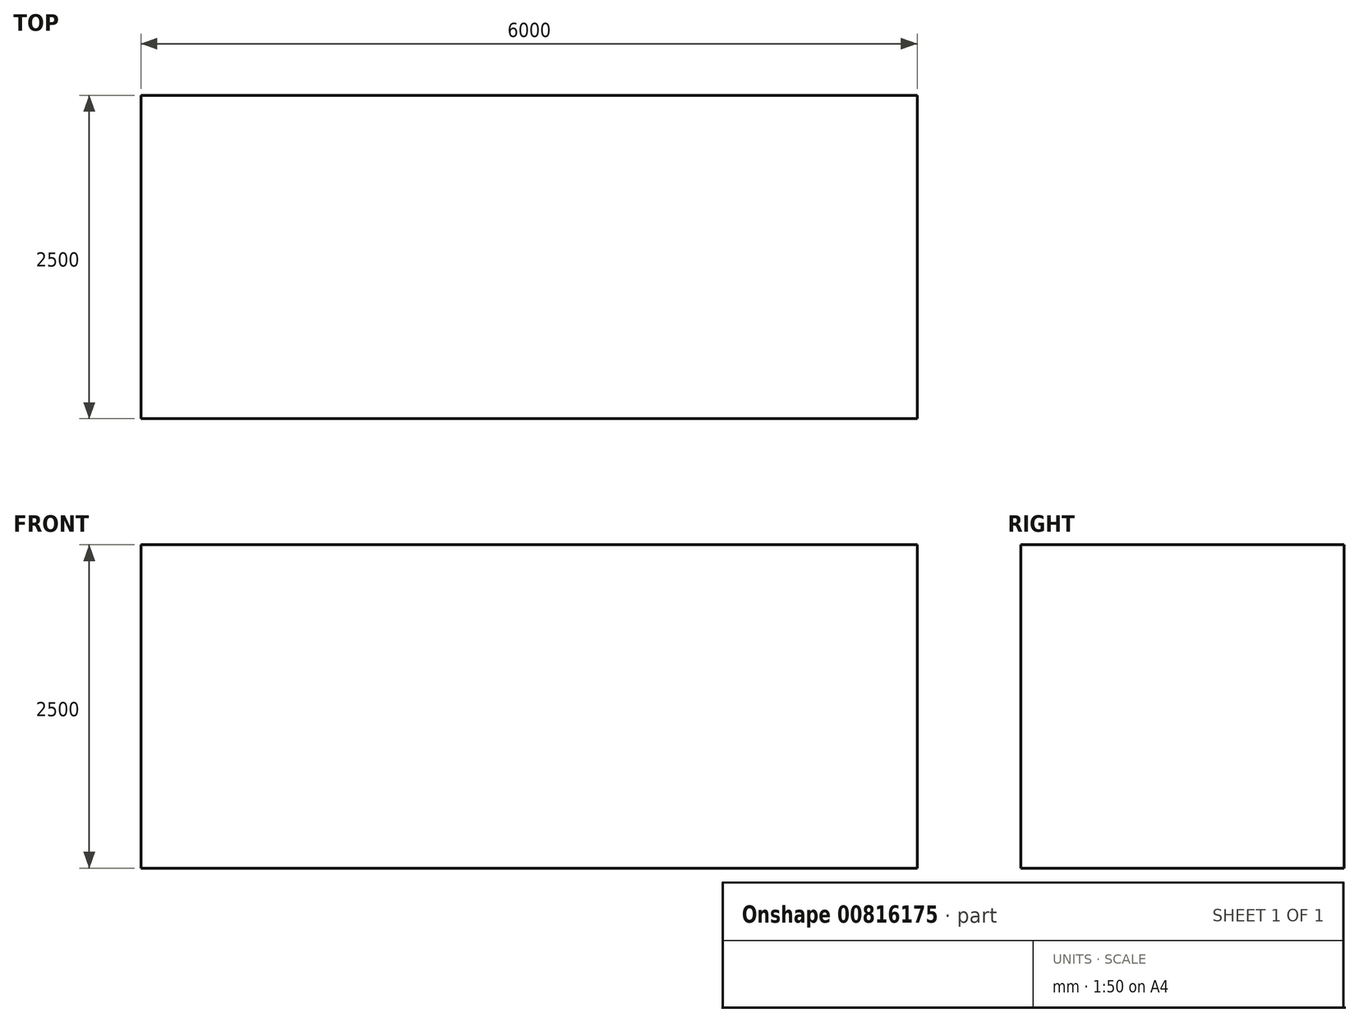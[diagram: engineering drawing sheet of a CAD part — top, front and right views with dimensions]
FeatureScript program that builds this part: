
annotation { "Feature Type Name" : "Feature", "Feature Type Description" : "" }
export const myFeature = defineFeature(function(context is Context, id is Id, definition is map)
    precondition{}
    {
        {
            var Q0;
            Q0=qCreatedBy(makeId("Top.planeOp"),FACE);
            var sketch = newSketch(context, id + "F0", { "sketchPlane" : qUnion([Q0])});
            skLineSegment(sketch, "E0.bottom", {"start": v(-3040.23, 1245.09) * mm, "end": v(2959.77, 1245.09) * mm});
            skLineSegment(sketch, "E0.top", {"start": v(-3040.23, -1254.91) * mm, "end": v(2959.77, -1254.91) * mm});
            skLineSegment(sketch, "E0.left", {"start": v(-3040.23, 1245.09) * mm, "end": v(-3040.23, -1254.91) * mm});
            skLineSegment(sketch, "E0.right", {"start": v(2959.77, 1245.09) * mm, "end": v(2959.77, -1254.91) * mm});
            skSolve(sketch);
        }
        {
            var Q0;
            Q0 = qSketchRegion(id + "F0", true);
            extrude(context, id + "F1", {"entities" : qUnion([Q0]), "depth" : 2500 * mm, "offsetDistance" : 25 * mm});
        }
        {
            var Q0;
            Q0=makeQuery(id+"F1.opExtrude","CAP_VERTEX",VERTEX,{"disambiguationData":[OSD([sQuery(id+"F0.wireOp",EDGE,"E0.bottom"),sQuery(id+"F0.wireOp",EDGE,"E0.left")])],"isStart":false});
            var Q1;
            Q1=makeQuery(id+"F1.opExtrude","CAP_VERTEX",VERTEX,{"disambiguationData":[OSD([sQuery(id+"F0.wireOp",EDGE,"E0.top"),sQuery(id+"F0.wireOp",EDGE,"E0.right")])],"isStart":false});
            var Q2;
            Q2=makeQuery(id+"F1.opExtrude","CAP_VERTEX",VERTEX,{"disambiguationData":[OSD([sQuery(id+"F0.wireOp",EDGE,"E0.top"),sQuery(id+"F0.wireOp",EDGE,"E0.right")])],"isStart":true});
            cPlane(context, id + "F2", {"entities" : qUnion([Q0, Q1, Q2]), "cplaneType" : CPlaneType.THREE_POINT, "offset" : 25 * mm, "width" : 150 * mm, "height" : 150 * mm});
        }
    });
